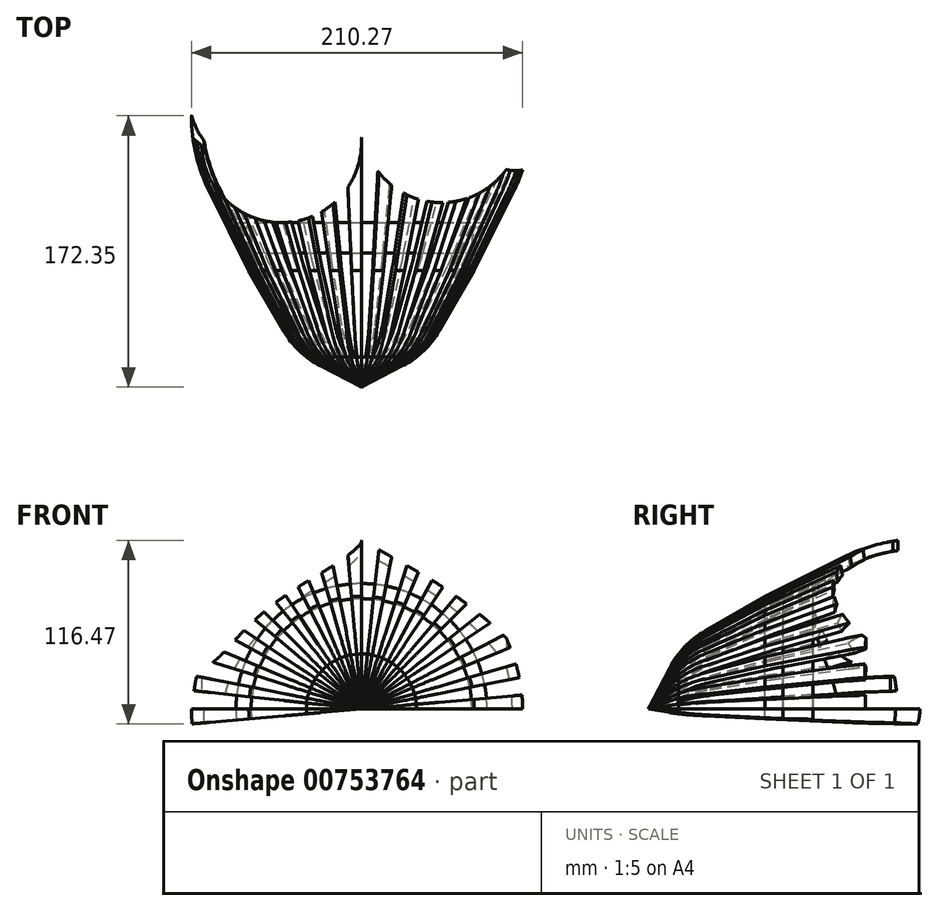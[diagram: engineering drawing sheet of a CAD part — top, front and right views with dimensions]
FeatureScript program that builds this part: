
annotation { "Feature Type Name" : "Feature", "Feature Type Description" : "" }
export const myFeature = defineFeature(function(context is Context, id is Id, definition is map)
    precondition{}
    {
        {
            var Q0;
            Q0=qCreatedBy(makeId("Top.planeOp"),FACE);
            var sketch = newSketch(context, id + "F0", { "sketchPlane" : qUnion([Q0])});
            skLineSegment(sketch, "E0", {"start": v(0, 118.64) * mm, "end": v(0, -97.26) * mm, "construction": true});
            skArc(sketch, "E1", {"start": v(66, -27.41) * mm, "mid": v(68.17, -23.36) * mm, "end": v(70.1, -19.2) * mm});
            skArc(sketch, "E2", {"start": v(23.27, -85.27) * mm, "mid": v(35.05, -76.88) * mm, "end": v(44, -65.51) * mm});
            skArc(sketch, "E3", {"start": v(0, 80.54) * mm, "mid": v(50.23, 55.14) * mm, "end": v(100.91, 79.64) * mm});
            skLineSegment(sketch, "E4", {"start": v(0, -97.26) * mm, "end": v(23.27, -85.27) * mm});
            skLineSegment(sketch, "E5", {"start": v(44, -65.51) * mm, "end": v(66, -27.41) * mm});
            skLineSegment(sketch, "E6", {"start": v(66, -27.41) * mm, "end": v(90.9, 22.44) * mm});
            skArc(sketch, "E7.trimOffspring", {"start": v(90.9, 22.44) * mm, "mid": v(100.08, 50.3) * mm, "end": v(100.91, 79.64) * mm});
            skPoint(sketch, "E8", {"position": v(0, 80.54) * mm});
            skArc(sketch, "E9.0", {"start": v(0, 92.46) * mm, "mid": v(53.5, 61.55) * mm, "end": v(103.84, 97.35) * mm});
            skArc(sketch, "E9.1", {"start": v(96.57, 19.6) * mm, "mid": v(107.48, 57.8) * mm, "end": v(103.84, 97.35) * mm});
            skLineSegment(sketch, "E9.2", {"start": v(0, -104.4) * mm, "end": v(26.18, -90.91) * mm});
            skArc(sketch, "E9.3", {"start": v(26.18, -90.91) * mm, "mid": v(39.44, -81.48) * mm, "end": v(49.5, -68.69) * mm});
            skLineSegment(sketch, "E9.4", {"start": v(49.5, -68.69) * mm, "end": v(71.59, -30.42) * mm});
            skLineSegment(sketch, "E9.5", {"start": v(71.59, -30.42) * mm, "end": v(96.57, 19.6) * mm});
            skLineSegment(sketch, "E10", {"start": v(0, -104.4) * mm, "end": v(0, -97.26) * mm});
            skLineSegment(sketch, "E11", {"start": v(0, 92.46) * mm, "end": v(0, 80.54) * mm});
            skLineSegment(sketch, "E12", {"start": v(100.91, 79.64) * mm, "end": v(103.84, 97.35) * mm});
            skLineSegment(sketch, "E13", {"start": v(0, 118.64) * mm, "end": v(0, -104.4) * mm, "construction": true});
            skLineSegment(sketch, "E14", {"start": v(23.27, -85.27) * mm, "end": v(0, -85.27) * mm});
            skLineSegment(sketch, "E15", {"start": v(0, -85.27) * mm, "end": v(0, -97.26) * mm});
            skLineSegment(sketch, "E16", {"start": v(70.1, -19.2) * mm, "end": v(70.1, 0) * mm});
            skLineSegment(sketch, "E17", {"start": v(70.1, 0) * mm, "end": v(79.68, 0) * mm});
            skLineSegment(sketch, "E18", {"start": v(23.27, -85.27) * mm, "end": v(35.03, -85.27) * mm});
            skSolve(sketch);
        }
        {
            var Q0;
            {var subQ2=sQuery(id+"F0.wireOp",EDGE,"E1");Q0=makeQuery(id+"F0.imprint","IMPRINT",FACE,{"disambiguationData":[TD([[makeQuery(id+"F0.imprint","IMPRINT",EDGE,{"derivedFrom":subQ2}),-1.0]])]});}
            var Q1;
            Q1=makeQuery(id+"F0.imprint","IMPRINT",FACE,{"disambiguationData":[TD([[makeQuery(id+"F0.imprint","IMPRINT",EDGE,{"derivedFrom":sQuery(id+"F0.wireOp",EDGE,"E4")}),-1.0]])]});
            var Q2;
            Q2=sQuery(id+"F0.wireOp",EDGE,"E0");
            revolve(context, id + "F1", {"surfaceOperationType" : NewSurfaceOperationType.NEW, "entities" : qUnion([Q0, Q1]), "axis" : qUnion([Q2]), "revolveType" : RevolveType.ONE_DIRECTION, "angle" : 5 * degree});
        }
        {
            var Q0;
            Q0=qCreatedBy(makeId("Top.planeOp"),FACE);
            var sketch = newSketch(context, id + "F2", { "sketchPlane" : qUnion([Q0])});
            skLineSegment(sketch, "E19", {"start": v(0, 130.44) * mm, "end": v(0, -109.9) * mm, "construction": true});
            skSolve(sketch);
        }
        {
            var Q0;
            Q0=makeQuery(id+"F1.opRevolve","SWEPT_BODY",BODY,{"disambiguationData":[OSD([sQuery(id+"F0.wireOp",EDGE,"E1"),sQuery(id+"F0.wireOp",EDGE,"E2"),sQuery(id+"F0.wireOp",EDGE,"E4"),sQuery(id+"F0.wireOp",EDGE,"E5"),sQuery(id+"F0.wireOp",EDGE,"E6"),sQuery(id+"F0.wireOp",EDGE,"E7.trimOffspring"),sQuery(id+"F0.wireOp",EDGE,"E9.1"),sQuery(id+"F0.wireOp",EDGE,"E9.2"),sQuery(id+"F0.wireOp",EDGE,"E9.3"),sQuery(id+"F0.wireOp",EDGE,"E9.4"),sQuery(id+"F0.wireOp",EDGE,"E9.5"),sQuery(id+"F0.wireOp",EDGE,"E10"),sQuery(id+"F0.wireOp",EDGE,"E12")])]});
            var Q1;
            Q1=sQuery(id+"F2.wireOp",EDGE,"E19");
            circularPattern(context, id + "F3", {"entities" : qUnion([Q0]), "axis" : qUnion([Q1]), "angle" : 180 * degree, "instanceCount" : 17, "equalSpace" : true});
        }
        {
            var Q0;
            {var subQ0=sQuery(id+"F0.wireOp",EDGE,"E16");Q0=makeQuery(id+"F0.imprint","IMPRINT",FACE,{"disambiguationData":[TD([[makeQuery(id+"F0.imprint","IMPRINT",EDGE,{"derivedFrom":subQ0}),-1.0]])]});}
            var Q1;
            Q1=makeQuery(id+"F0.imprint","IMPRINT",FACE,{"disambiguationData":[TD([[makeQuery(id+"F0.imprint","IMPRINT",EDGE,{"derivedFrom":sQuery(id+"F0.wireOp",EDGE,"E4")}),1.0]])]});
            var Q2;
            Q2=makeQuery(id+"F0.imprint","IMPRINT",FACE,{"disambiguationData":[TD([[makeQuery(id+"F0.imprint","IMPRINT",EDGE,{"derivedFrom":sQuery(id+"F0.wireOp",EDGE,"E4")}),-1.0]])]});
            var Q3;
            Q3=sQuery(id+"F0.wireOp",EDGE,"E13");
            revolve(context, id + "F4", {"surfaceOperationType" : NewSurfaceOperationType.NEW, "entities" : qUnion([Q0, Q1, Q2]), "axis" : qUnion([Q3]), "revolveType" : RevolveType.ONE_DIRECTION, "angle" : 185 * degree});
        }
        {
            var Q0;
            Q0=makeQuery(id+"F4.opRevolve","SWEPT_EDGE",EDGE,{"disambiguationData":[OSD([sQuery(id+"F0.wireOp",EDGE,"E16"),sQuery(id+"F0.wireOp",EDGE,"E17")])]});
            fillet(context, id + "F5", {"entities" : qUnion([Q0]), "radius" : 12.7 * mm, "tangentPropagation" : true, "allowEdgeOverflow" : false});
        }
        {
            var Q0;
            Q0=qCreatedBy(makeId("Top.planeOp"),FACE);
            var sketch = newSketch(context, id + "F6", { "sketchPlane" : qUnion([Q0])});
            skLineSegment(sketch, "E20", {"start": v(0, 99.99) * mm, "end": v(0, -113.41) * mm, "construction": true});
            skPoint(sketch, "E21", {"position": v(84.41, -172.35) * mm});
            skLineSegment(sketch, "E22", {"start": v(-67.48, 0) * mm, "end": v(69.53, 0) * mm, "construction": true});
            skCircle(sketch, "E23", {"center": v(50.8, 50.8) * mm, "radius": 50.8 * mm});
            skCircle(sketch, "E24", {"center": v(-50.8, 50.8) * mm, "radius": 50.8 * mm});
            skCircle(sketch, "E25", {"center": v(0, 99.99) * mm, "radius": 46.01 * mm});
            skCircle(sketch, "E26", {"center": v(63.5, 99.99) * mm, "radius": 63.5 * mm});
            skCircle(sketch, "E27", {"center": v(-63.5, 99.99) * mm, "radius": 63.5 * mm});
            skCircle(sketch, "E28", {"center": v(50.8, 63.5) * mm, "radius": 50.8 * mm});
            skSolve(sketch);
        }
        {
            var Q0;
            {var subQ0=sQuery(id+"F6.wireOp",EDGE,"E25");var subQ1=sQuery(id+"F6.wireOp",EDGE,"E23");var subQ2=makeQuery(id+"F6.imprint","INTERSECT",VERTEX,{"disambiguationData":[OD(0.0)],"derivedFrom":[subQ1,subQ0]});Q0=makeQuery(id+"F6.imprint","IMPRINT",FACE,{"disambiguationData":[TD([[makeQuery(id+"F6.imprint","IMPRINT",EDGE,{"disambiguationData":[TD([[subQ2,1.0]])],"derivedFrom":subQ1}),1.0]])]});}
            var Q1;
            {var subQ0=sQuery(id+"F6.wireOp",EDGE,"E25");var subQ1=sQuery(id+"F6.wireOp",EDGE,"E23");var subQ2=makeQuery(id+"F6.imprint","INTERSECT",VERTEX,{"disambiguationData":[OD(0.0)],"derivedFrom":[subQ1,subQ0]});Q1=makeQuery(id+"F6.imprint","IMPRINT",FACE,{"disambiguationData":[TD([[makeQuery(id+"F6.imprint","IMPRINT",EDGE,{"disambiguationData":[TD([[subQ2,-1.0]])],"derivedFrom":subQ1}),1.0]])]});}
            var Q2;
            {var subQ0=sQuery(id+"F6.wireOp",EDGE,"E25");var subQ1=sQuery(id+"F6.wireOp",EDGE,"E23");var subQ2=makeQuery(id+"F6.imprint","INTERSECT",VERTEX,{"disambiguationData":[OD(0.0)],"derivedFrom":[subQ1,subQ0]});Q2=makeQuery(id+"F6.imprint","IMPRINT",FACE,{"disambiguationData":[TD([[makeQuery(id+"F6.imprint","IMPRINT",EDGE,{"disambiguationData":[TD([[subQ2,1.0]])],"derivedFrom":subQ1}),-1.0]])]});}
            var Q3;
            {var subQ0=sQuery(id+"F6.wireOp",EDGE,"E28");var subQ1=sQuery(id+"F6.wireOp",EDGE,"E25");var subQ2=makeQuery(id+"F6.imprint","INTERSECT",VERTEX,{"disambiguationData":[OD(1.0)],"derivedFrom":[subQ1,subQ0]});Q3=makeQuery(id+"F6.imprint","IMPRINT",FACE,{"disambiguationData":[TD([[makeQuery(id+"F6.imprint","IMPRINT",EDGE,{"disambiguationData":[TD([[subQ2,-1.0]])],"derivedFrom":subQ1}),-1.0]])]});}
            var Q4;
            {var subQ0=sQuery(id+"F6.wireOp",EDGE,"E26");var subQ1=sQuery(id+"F6.wireOp",EDGE,"E25");var subQ2=makeQuery(id+"F6.imprint","INTERSECT",VERTEX,{"disambiguationData":[OD(0.0)],"derivedFrom":[subQ1,subQ0]});Q4=makeQuery(id+"F6.imprint","IMPRINT",FACE,{"disambiguationData":[TD([[makeQuery(id+"F6.imprint","IMPRINT",EDGE,{"disambiguationData":[TD([[subQ2,1.0]])],"derivedFrom":subQ1}),1.0]])]});}
            var Q5;
            {var subQ0=sQuery(id+"F6.wireOp",EDGE,"E25");var subQ1=sQuery(id+"F6.wireOp",EDGE,"E23");var subQ2=makeQuery(id+"F6.imprint","INTERSECT",VERTEX,{"disambiguationData":[OD(0.0)],"derivedFrom":[subQ1,subQ0]});Q5=makeQuery(id+"F6.imprint","IMPRINT",FACE,{"disambiguationData":[TD([[makeQuery(id+"F6.imprint","IMPRINT",EDGE,{"disambiguationData":[TD([[subQ2,-1.0]])],"derivedFrom":subQ1}),-1.0]])]});}
            var Q6;
            {var subQ0=sQuery(id+"F6.wireOp",EDGE,"E26");var subQ1=sQuery(id+"F6.wireOp",EDGE,"E23");var subQ2=makeQuery(id+"F6.imprint","INTERSECT",VERTEX,{"disambiguationData":[OD(0.0)],"derivedFrom":[subQ1,subQ0]});Q6=makeQuery(id+"F6.imprint","IMPRINT",FACE,{"disambiguationData":[TD([[makeQuery(id+"F6.imprint","IMPRINT",EDGE,{"disambiguationData":[TD([[subQ2,-1.0]])],"derivedFrom":subQ1}),-1.0]])]});}
            var Q7;
            {var subQ0=sQuery(id+"F6.wireOp",EDGE,"E24");var subQ1=makeQuery(id+"F6.imprint","INTERSECT",VERTEX,{"derivedFrom":[sQuery(id+"F6.wireOp",EDGE,"E23"),subQ0]});Q7=makeQuery(id+"F6.imprint","IMPRINT",FACE,{"disambiguationData":[TD([[makeQuery(id+"F6.imprint","IMPRINT",EDGE,{"disambiguationData":[TD([[subQ1,-1.0]])],"derivedFrom":subQ0}),1.0]])]});}
            var Q8;
            {var subQ0=sQuery(id+"F6.wireOp",EDGE,"E27");var subQ1=sQuery(id+"F6.wireOp",EDGE,"E24");var subQ2=makeQuery(id+"F6.imprint","INTERSECT",VERTEX,{"disambiguationData":[OD(0.0)],"derivedFrom":[subQ1,subQ0]});Q8=makeQuery(id+"F6.imprint","IMPRINT",FACE,{"disambiguationData":[TD([[makeQuery(id+"F6.imprint","IMPRINT",EDGE,{"disambiguationData":[TD([[subQ2,1.0]])],"derivedFrom":subQ1}),1.0]])]});}
            var Q9;
            {var subQ0=sQuery(id+"F6.wireOp",EDGE,"E27");var subQ1=sQuery(id+"F6.wireOp",EDGE,"E24");var subQ2=makeQuery(id+"F6.imprint","INTERSECT",VERTEX,{"disambiguationData":[OD(1.0)],"derivedFrom":[subQ1,subQ0]});Q9=makeQuery(id+"F6.imprint","IMPRINT",FACE,{"disambiguationData":[TD([[makeQuery(id+"F6.imprint","IMPRINT",EDGE,{"disambiguationData":[TD([[subQ2,-1.0]])],"derivedFrom":subQ1}),1.0]])]});}
            var Q10;
            {var subQ0=sQuery(id+"F6.wireOp",EDGE,"E25");var subQ1=sQuery(id+"F6.wireOp",EDGE,"E24");var subQ2=makeQuery(id+"F6.imprint","INTERSECT",VERTEX,{"disambiguationData":[OD(0.0)],"derivedFrom":[subQ1,subQ0]});Q10=makeQuery(id+"F6.imprint","IMPRINT",FACE,{"disambiguationData":[TD([[makeQuery(id+"F6.imprint","IMPRINT",EDGE,{"disambiguationData":[TD([[subQ2,-1.0]])],"derivedFrom":subQ1}),1.0]])]});}
            var Q11;
            {var subQ0=sQuery(id+"F6.wireOp",EDGE,"E27");var subQ1=sQuery(id+"F6.wireOp",EDGE,"E24");var subQ2=makeQuery(id+"F6.imprint","INTERSECT",VERTEX,{"disambiguationData":[OD(1.0)],"derivedFrom":[subQ1,subQ0]});Q11=makeQuery(id+"F6.imprint","IMPRINT",FACE,{"disambiguationData":[TD([[makeQuery(id+"F6.imprint","IMPRINT",EDGE,{"disambiguationData":[TD([[subQ2,-1.0]])],"derivedFrom":subQ1}),-1.0]])]});}
            var Q12;
            {var subQ0=sQuery(id+"F6.wireOp",EDGE,"E27");var subQ1=sQuery(id+"F6.wireOp",EDGE,"E24");var subQ2=makeQuery(id+"F6.imprint","INTERSECT",VERTEX,{"disambiguationData":[OD(0.0)],"derivedFrom":[subQ1,subQ0]});Q12=makeQuery(id+"F6.imprint","IMPRINT",FACE,{"disambiguationData":[TD([[makeQuery(id+"F6.imprint","IMPRINT",EDGE,{"disambiguationData":[TD([[subQ2,1.0]])],"derivedFrom":subQ1}),-1.0]])]});}
            var Q13;
            {var subQ0=sQuery(id+"F6.wireOp",EDGE,"E26");var subQ1=sQuery(id+"F6.wireOp",EDGE,"E23");var subQ2=makeQuery(id+"F6.imprint","INTERSECT",VERTEX,{"disambiguationData":[OD(1.0)],"derivedFrom":[subQ1,subQ0]});Q13=makeQuery(id+"F6.imprint","IMPRINT",FACE,{"disambiguationData":[TD([[makeQuery(id+"F6.imprint","IMPRINT",EDGE,{"disambiguationData":[TD([[subQ2,-1.0]])],"derivedFrom":subQ1}),1.0]])]});}
            var Q14;
            {var subQ0=sQuery(id+"F6.wireOp",EDGE,"E26");var subQ1=sQuery(id+"F6.wireOp",EDGE,"E23");var subQ2=makeQuery(id+"F6.imprint","INTERSECT",VERTEX,{"disambiguationData":[OD(1.0)],"derivedFrom":[subQ1,subQ0]});Q14=makeQuery(id+"F6.imprint","IMPRINT",FACE,{"disambiguationData":[TD([[makeQuery(id+"F6.imprint","IMPRINT",EDGE,{"disambiguationData":[TD([[subQ2,-1.0]])],"derivedFrom":subQ1}),-1.0]])]});}
            var Q15;
            {var subQ3=sQuery(id+"F6.wireOp",EDGE,"E28");var subQ6=sQuery(id+"F6.wireOp",EDGE,"E23");var subQ11=makeQuery(id+"F6.imprint","INTERSECT",VERTEX,{"disambiguationData":[OD(1.0)],"derivedFrom":[subQ6,subQ3]});Q15=makeQuery(id+"F6.imprint","IMPRINT",FACE,{"disambiguationData":[TD([[makeQuery(id+"F6.imprint","IMPRINT",EDGE,{"disambiguationData":[TD([[subQ11,-1.0]])],"derivedFrom":subQ6}),-1.0]])]});}
            extrude(context, id + "F7", {"entities" : qUnion([Q0, Q1, Q2, Q3, Q4, Q5, Q6, Q7, Q8, Q9, Q10, Q11, Q12, Q13, Q14, Q15]), "operationType" : NewBodyOperationType.REMOVE, "endBound" : BoundingType.THROUGH_ALL, "depth" : 25.4 * mm, "offsetDistance" : 25.4 * mm});
        }
        {
            var Q0;
            Q0=qCreatedBy(makeId("Top.planeOp"),FACE);
            var sketch = newSketch(context, id + "F8", { "sketchPlane" : qUnion([Q0])});
            skCircle(sketch, "E29", {"center": v(97.65, 54.98) * mm, "radius": 22.04 * mm});
            skCircle(sketch, "E30", {"center": v(-59.85, 81.7) * mm, "radius": 50.03 * mm});
            skSolve(sketch);
        }
        {
            var Q0;
            Q0=makeQuery(id+"F8.imprint","IMPRINT",FACE,{"disambiguationData":[TD([[makeQuery(id+"F8.imprint","IMPRINT",EDGE,{"derivedFrom":sQuery(id+"F8.wireOp",EDGE,"E30")}),1.0]])]});
            var Q1;
            Q1=makeQuery(id+"F8.imprint","IMPRINT",FACE,{"disambiguationData":[TD([[makeQuery(id+"F8.imprint","IMPRINT",EDGE,{"derivedFrom":sQuery(id+"F8.wireOp",EDGE,"E29")}),1.0]])]});
            extrude(context, id + "F9", {"entities" : qUnion([Q0, Q1]), "operationType" : NewBodyOperationType.REMOVE, "endBound" : BoundingType.THROUGH_ALL, "depth" : 25.4 * mm, "offsetDistance" : 25.4 * mm});
        }
        {
            var Q0;
            Q0=makeQuery(id+"F8.imprint","IMPRINT",FACE,{"disambiguationData":[TD([[makeQuery(id+"F8.imprint","IMPRINT",EDGE,{"derivedFrom":sQuery(id+"F8.wireOp",EDGE,"E30")}),1.0]])]});
            extrude(context, id + "F10", {"entities" : qUnion([Q0]), "operationType" : NewBodyOperationType.REMOVE, "endBound" : BoundingType.THROUGH_ALL, "oppositeDirection" : true, "depth" : 25.4 * mm, "offsetDistance" : 25.4 * mm});
        }
    });
